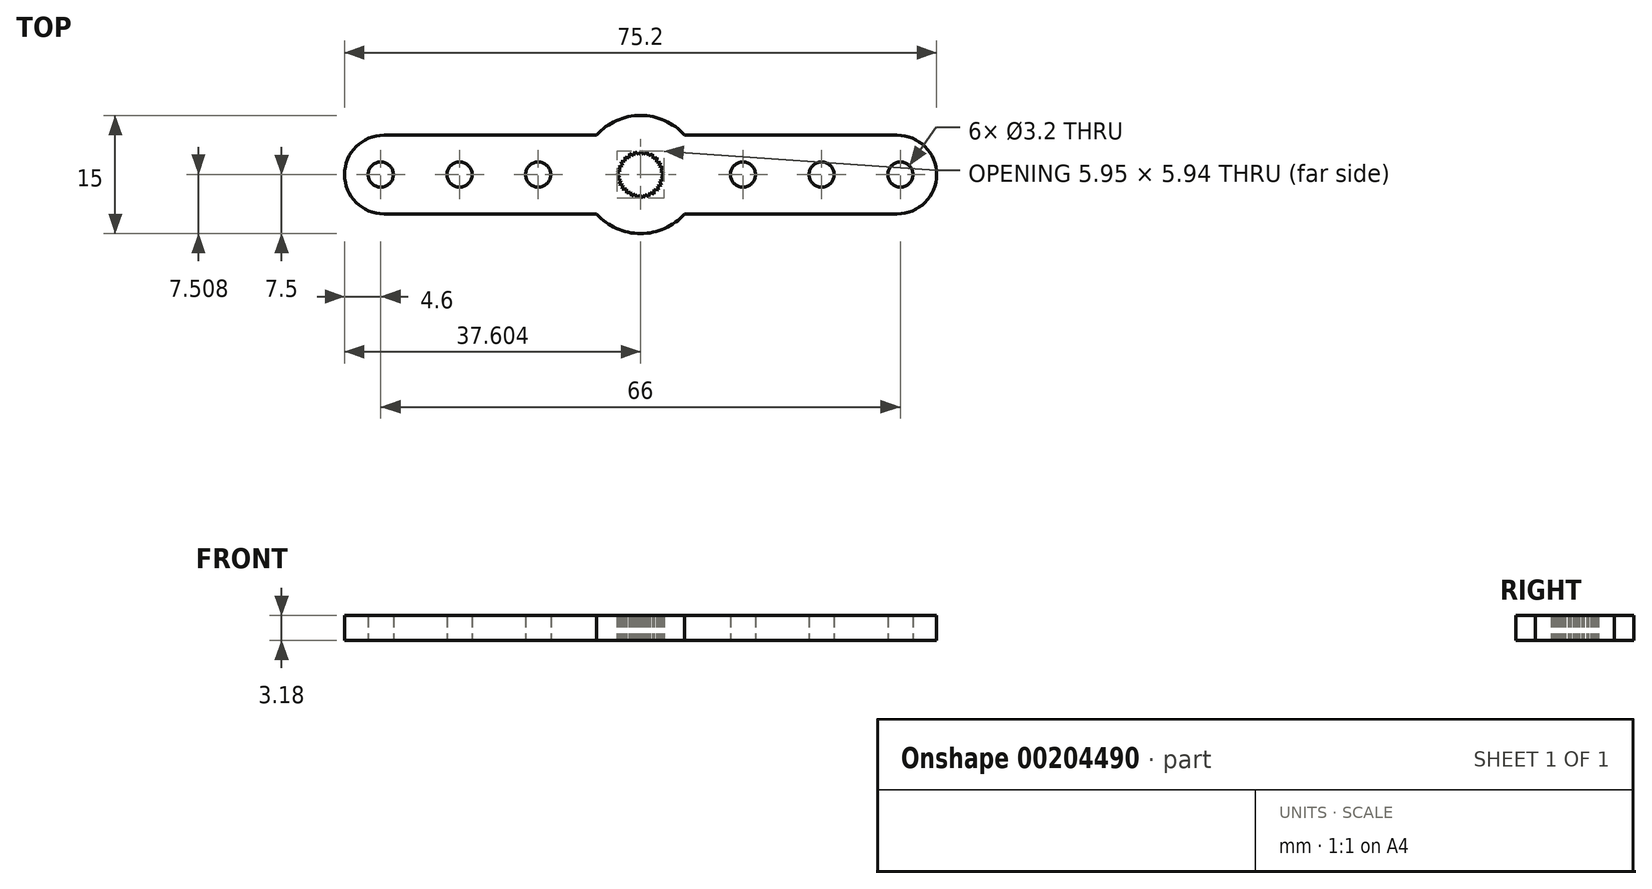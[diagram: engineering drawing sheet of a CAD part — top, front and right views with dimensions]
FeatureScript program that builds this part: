
annotation { "Feature Type Name" : "Feature", "Feature Type Description" : "" }
export const myFeature = defineFeature(function(context is Context, id is Id, definition is map)
    precondition{}
    {
        {
            var Q0;
            Q0=qCreatedBy(makeId("Top.planeOp"),FACE);
            var sketch = newSketch(context, id + "F0", { "sketchPlane" : qUnion([Q0])});
            skLineSegment(sketch, "E0.bottom", {"start": v(-5.6, 5) * mm, "end": v(-32.6, 5) * mm});
            skLineSegment(sketch, "E0.top", {"start": v(-5.6, -5) * mm, "end": v(-32.6, -5) * mm});
            skCircle(sketch, "E1", {"center": v(-33, 0) * mm, "radius": 1.6 * mm});
            skCircle(sketch, "E2.1.0.0", {"center": v(-23, 0) * mm, "radius": 1.6 * mm});
            skCircle(sketch, "E2.2.0.0", {"center": v(-13, 0) * mm, "radius": 1.6 * mm});
            skLineSegment(sketch, "E2.direction1", {"start": v(-33, 0) * mm, "end": v(-23, 0) * mm, "construction": true});
            skArc(sketch, "E3", {"start": v(-32.6, 5) * mm, "mid": v(-36.14, 3.54) * mm, "end": v(-37.6, 0) * mm});
            skArc(sketch, "E4.MirrorCS", {"start": v(-32.6, -5) * mm, "mid": v(-36.14, -3.54) * mm, "end": v(-37.6, 0) * mm});
            skLineSegment(sketch, "E5.MirrorCS", {"start": v(5.6, 5) * mm, "end": v(32.6, 5) * mm});
            skLineSegment(sketch, "E6.MirrorCS", {"start": v(5.6, -5) * mm, "end": v(32.6, -5) * mm});
            skArc(sketch, "E7.MirrorCS", {"start": v(32.6, -5) * mm, "mid": v(36.14, -3.54) * mm, "end": v(37.6, 0) * mm});
            skCircle(sketch, "E8.MirrorC", {"center": v(23, 0) * mm, "radius": 1.6 * mm});
            skCircle(sketch, "E9.MirrorC", {"center": v(33, 0) * mm, "radius": 1.6 * mm});
            skCircle(sketch, "E10.MirrorC", {"center": v(13, 0) * mm, "radius": 1.6 * mm});
            skArc(sketch, "E11.MirrorCS", {"start": v(32.6, 5) * mm, "mid": v(36.14, 3.54) * mm, "end": v(37.6, 0) * mm});
            skLineSegment(sketch, "E12.MirrorCS", {"start": v(33, 0) * mm, "end": v(23, 0) * mm, "construction": true});
            skLineSegment(sketch, "E13", {"start": v(-2.48, 1.65) * mm, "end": v(-2.31, 1.15) * mm});
            skLineSegment(sketch, "E14", {"start": v(-2.31, 1.15) * mm, "end": v(-2.81, 0.98) * mm});
            skLineSegment(sketch, "E15.1.0", {"start": v(-2.81, 0.98) * mm, "end": v(-2.53, 0.54) * mm});
            skLineSegment(sketch, "E15.1.1", {"start": v(-2.53, 0.54) * mm, "end": v(-2.97, 0.25) * mm});
            skLineSegment(sketch, "E15.2.0", {"start": v(-2.97, 0.25) * mm, "end": v(-2.58, -0.1) * mm});
            skLineSegment(sketch, "E15.2.1", {"start": v(-2.58, -0.1) * mm, "end": v(-2.94, -0.5) * mm});
            skLineSegment(sketch, "E15.3.0", {"start": v(-2.94, -0.5) * mm, "end": v(-2.47, -0.74) * mm});
            skLineSegment(sketch, "E15.3.1", {"start": v(-2.47, -0.74) * mm, "end": v(-2.72, -1.2) * mm});
            skLineSegment(sketch, "E15.4.0", {"start": v(-2.72, -1.2) * mm, "end": v(-2.21, -1.34) * mm});
            skLineSegment(sketch, "E15.4.1", {"start": v(-2.21, -1.34) * mm, "end": v(-2.34, -1.85) * mm});
            skLineSegment(sketch, "E15.5.0", {"start": v(-2.34, -1.85) * mm, "end": v(-1.8, -1.84) * mm});
            skLineSegment(sketch, "E15.5.1", {"start": v(-1.8, -1.84) * mm, "end": v(-1.8, -2.37) * mm});
            skLineSegment(sketch, "E15.6.0", {"start": v(-1.8, -2.37) * mm, "end": v(-1.3, -2.24) * mm});
            skLineSegment(sketch, "E15.6.1", {"start": v(-1.3, -2.24) * mm, "end": v(-1.16, -2.75) * mm});
            skLineSegment(sketch, "E15.7.0", {"start": v(-1.16, -2.75) * mm, "end": v(-0.7, -2.49) * mm});
            skLineSegment(sketch, "E15.7.1", {"start": v(-0.7, -2.49) * mm, "end": v(-0.44, -2.95) * mm});
            skLineSegment(sketch, "E15.8.0", {"start": v(-0.44, -2.95) * mm, "end": v(-0.06, -2.58) * mm});
            skLineSegment(sketch, "E15.8.1", {"start": v(-0.06, -2.58) * mm, "end": v(0.3, -2.96) * mm});
            skLineSegment(sketch, "E15.9.0", {"start": v(0.3, -2.96) * mm, "end": v(0.59, -2.52) * mm});
            skLineSegment(sketch, "E15.9.1", {"start": v(0.59, -2.52) * mm, "end": v(1.04, -2.8) * mm});
            skLineSegment(sketch, "E15.10.0", {"start": v(1.04, -2.8) * mm, "end": v(1.2, -2.3) * mm});
            skLineSegment(sketch, "E15.10.1", {"start": v(1.2, -2.3) * mm, "end": v(1.7, -2.45) * mm});
            skLineSegment(sketch, "E15.11.0", {"start": v(1.7, -2.45) * mm, "end": v(1.73, -1.92) * mm});
            skLineSegment(sketch, "E15.11.1", {"start": v(1.73, -1.92) * mm, "end": v(2.25, -1.95) * mm});
            skLineSegment(sketch, "E15.12.0", {"start": v(2.25, -1.95) * mm, "end": v(2.15, -1.43) * mm});
            skLineSegment(sketch, "E15.12.1", {"start": v(2.15, -1.43) * mm, "end": v(2.67, -1.33) * mm});
            skLineSegment(sketch, "E15.13.0", {"start": v(2.67, -1.33) * mm, "end": v(2.44, -0.85) * mm});
            skLineSegment(sketch, "E15.13.1", {"start": v(2.44, -0.85) * mm, "end": v(2.91, -0.62) * mm});
            skLineSegment(sketch, "E15.14.0", {"start": v(2.91, -0.62) * mm, "end": v(2.57, -0.22) * mm});
            skLineSegment(sketch, "E15.14.1", {"start": v(2.57, -0.22) * mm, "end": v(2.98, 0.12) * mm});
            skLineSegment(sketch, "E15.15.0", {"start": v(2.98, 0.12) * mm, "end": v(2.55, 0.43) * mm});
            skLineSegment(sketch, "E15.15.1", {"start": v(2.55, 0.43) * mm, "end": v(2.85, 0.86) * mm});
            skLineSegment(sketch, "E15.16.0", {"start": v(2.85, 0.86) * mm, "end": v(2.36, 1.05) * mm});
            skLineSegment(sketch, "E15.16.1", {"start": v(2.36, 1.05) * mm, "end": v(2.55, 1.54) * mm});
            skLineSegment(sketch, "E15.17.0", {"start": v(2.55, 1.54) * mm, "end": v(2.03, 1.6) * mm});
            skLineSegment(sketch, "E15.17.1", {"start": v(2.03, 1.6) * mm, "end": v(2.09, 2.13) * mm});
            skLineSegment(sketch, "E15.18.0", {"start": v(2.09, 2.13) * mm, "end": v(1.56, 2.06) * mm});
            skLineSegment(sketch, "E15.18.1", {"start": v(1.56, 2.06) * mm, "end": v(1.5, 2.58) * mm});
            skLineSegment(sketch, "E15.19.0", {"start": v(1.5, 2.58) * mm, "end": v(1, 2.38) * mm});
            skLineSegment(sketch, "E15.19.1", {"start": v(1, 2.38) * mm, "end": v(0.8, 2.87) * mm});
            skLineSegment(sketch, "E15.20.0", {"start": v(0.8, 2.87) * mm, "end": v(0.38, 2.56) * mm});
            skLineSegment(sketch, "E15.20.1", {"start": v(0.38, 2.56) * mm, "end": v(0.07, 2.98) * mm});
            skLineSegment(sketch, "E15.21.0", {"start": v(0.07, 2.98) * mm, "end": v(-0.27, 2.57) * mm});
            skLineSegment(sketch, "E15.21.1", {"start": v(-0.27, 2.57) * mm, "end": v(-0.68, 2.9) * mm});
            skLineSegment(sketch, "E15.22.0", {"start": v(-0.68, 2.9) * mm, "end": v(-0.9, 2.42) * mm});
            skLineSegment(sketch, "E15.22.1", {"start": v(-0.9, 2.42) * mm, "end": v(-1.38, 2.64) * mm});
            skLineSegment(sketch, "E15.23.0", {"start": v(-1.38, 2.64) * mm, "end": v(-1.47, 2.12) * mm});
            skLineSegment(sketch, "E15.23.1", {"start": v(-1.47, 2.12) * mm, "end": v(-2, 2.22) * mm});
            skLineSegment(sketch, "E15.24.0", {"start": v(-2, 2.22) * mm, "end": v(-1.95, 1.69) * mm});
            skLineSegment(sketch, "E15.24.1", {"start": v(-1.95, 1.69) * mm, "end": v(-2.48, 1.65) * mm});
            skPoint(sketch, "E15.center", {"position": v(0, 0) * mm});
            skArc(sketch, "E16", {"start": v(-5.6, -5) * mm, "mid": v(0, -7.5) * mm, "end": v(5.6, -5) * mm});
            skPoint(sketch, "E17.orphan", {"position": v(0, 5) * mm});
            skPoint(sketch, "E18.orphan", {"position": v(0, -5) * mm});
            skArc(sketch, "E19.trimOffspring", {"start": v(5.6, 5) * mm, "mid": v(0, 7.5) * mm, "end": v(-5.6, 5) * mm});
            skSolve(sketch);
        }
        {
            var Q0;
            Q0=makeQuery(id+"F0.imprint","IMPRINT",FACE,{"disambiguationData":[TD([[makeQuery(id+"F0.imprint","IMPRINT",EDGE,{"derivedFrom":sQuery(id+"F0.wireOp",EDGE,"E2.2.0.0")}),-1.0]])]});
            extrude(context, id + "F1", {"entities" : qUnion([Q0]), "depth" : 3.17 * mm});
        }
    });
